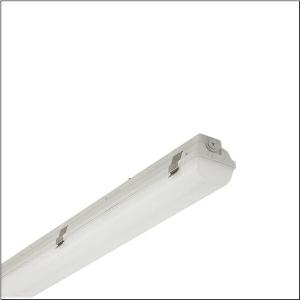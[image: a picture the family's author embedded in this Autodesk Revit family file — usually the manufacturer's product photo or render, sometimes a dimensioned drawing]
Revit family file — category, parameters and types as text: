
# Revit family: monsun_r__21_eco_51fj10mp47a_2b6f
name_source: partatom
category: Lighting Fixtures
units: mm (PartAtom-declared; Revit-internal decimal feet)

## family parameters
Cut with Voids When Loaded = No
Host = Face
Light Source = No
Part Type = Normal
Room Calculation Point = No
Round Connector Dimension = Use Diameter
Shared = No

## types (1)
- --- (1 x LED, 7000 lm, 50 W, 4000K)
    Apparent Load = 50 VA
    CIE Flux Codes = 41 70 89 90 100
    Color Rendering = 80
    Color Temperature = 4000K
    Default Elevation = 1800 mm
    Description = Monsun® 21 Eco, damp-proof luminaire, primary optical cover: diffuser, of PMMA, frosted, light emission: direct distribution, primary light characteristic: symmetric, installation type: suspended mounting, surface-mounted, LED, rated luminous flux: 7.000lm, luminous efficacy: 140lm/W, light colour: 840, colour temperature: 4000K, control gear: ECG Multilumen, with terminal, 3-pole, max. 2.5mm², mains connection: 220..240V, AC, 50/60Hz, rated input power: 50W, housing, of glass-fibre reinforced polyester, light grey (RAL 7035), length: 1.577mm, width: 90mm, height: 95mm, clip for enclosure, of spring steel V2A, protection rating (complete): IP66, insulation class (complete): insulation class I (protective earthing), certification: CE, UKCA, protection symbol: D, impact resistance: IK02, permissible operating ambient temperature: -20..+35°C, corresponds to IFS (International Featured Standards) requirements for safety and quality in the food industry, contact your sales advisor before using the luminaires in applications with unclear chemical exposure, large temperature fluctuations or condensation-forming humidity, packaging unit: 1 piece
    Height = 103 mm
    Lamp = 1 x LED
    Lamp Light Flux = 7000 lm
    Lamp Power = 50 W
    Lamp count = 1
    Length = 1577 mm
    Luminous efficacy = 140 lm/W
    Manufacturer = Siteco
    ModVariant = No
    Model = 51FJ10MP47A
    Mounting Place = Ceiling
    Mounting Type = Surface mounted
    Number of Poles = 1
    OnlyDefault = Yes
    Power Factor = 1
    Product Name = Monsun® 21 Eco
    Product group = damp-proof luminaire
    ProductGroupID = 300
    Protection Class = Protection class I
    Protection Degree = IP 66
    RLX_Detail_Level = 1
    RLX_Emergency_Light_Flux = 0 lm
    RLX_Emergency_Type = 0
    RLX_Emergency_Type_DB = No
    RlxData = <blob elided: 34093 chars, md5=392c3787>
    Socket = socket
    Standby Power = 0 W
    System Light Flux = 7000 lm
    System Power = 50 W
    Type Comments = factory setting: luminous flux: 100 % | (ON | ON | ON | ON) | 350 mA
    Type Image = l_1007218.jpg
    URL = http://relux.com
    VarID = @adj_116131
    Voltage = 0 V
    Weight = 0.00 kg
    Width = 90 mm

## geometry (parser evidence)
native form markers: Blend x4, Sweep x13
no freeform markers — native parametric forms only
